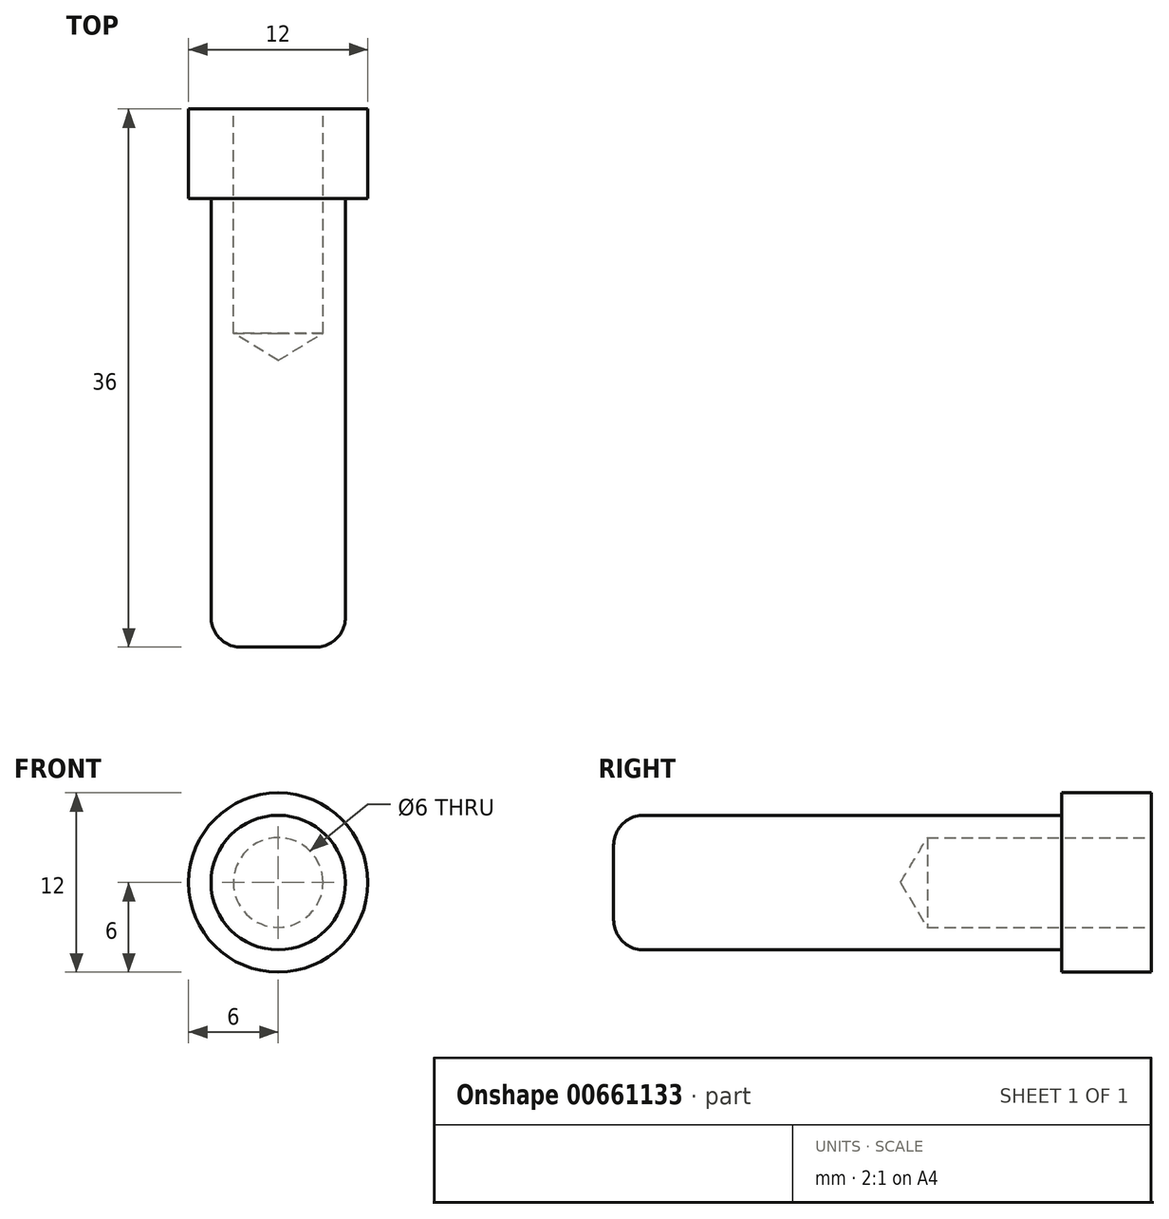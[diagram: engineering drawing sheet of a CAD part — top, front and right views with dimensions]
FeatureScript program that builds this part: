
annotation { "Feature Type Name" : "Feature", "Feature Type Description" : "" }
export const myFeature = defineFeature(function(context is Context, id is Id, definition is map)
    precondition{}
    {
        {
            var Q0;
            Q0=qCreatedBy(makeId("Front.planeOp"),FACE);
            var sketch = newSketch(context, id + "F0", { "sketchPlane" : qUnion([Q0])});
            skCircle(sketch, "E0", {"center": v(0, 0) * mm, "radius": 6 * mm});
            skSolve(sketch);
        }
        {
            var Q0;
            Q0 = qSketchRegion(id + "F0", true);
            extrude(context, id + "F1", {"entities" : qUnion([Q0]), "depth" : 6 * mm, "offsetDistance" : 25 * mm});
        }
        {
            var Q0;
            Q0=makeQuery(id+"F1.opExtrude","CAP_FACE",FACE,{"disambiguationData":[OSD([sQuery(id+"F0.wireOp",EDGE,"E0")])],"isStart":false});
            var sketch = newSketch(context, id + "F2", { "sketchPlane" : qUnion([Q0])});
            skCircle(sketch, "E1", {"center": v(0, 0) * mm, "radius": 4.5 * mm});
            skSolve(sketch);
        }
        {
            var Q0;
            Q0=makeQuery(id+"F2.imprint","IMPRINT",FACE,{"disambiguationData":[TD([[makeQuery(id+"F2.imprint","IMPRINT",EDGE,{"derivedFrom":sQuery(id+"F2.wireOp",EDGE,"E1")}),1.0]])]});
            extrude(context, id + "F3", {"entities" : qUnion([Q0]), "operationType" : NewBodyOperationType.ADD, "depth" : 30 * mm, "offsetDistance" : 25 * mm});
        }
        {
            var Q0;
            Q0=makeQuery(id+"F3.opExtrude","CAP_EDGE",EDGE,{"disambiguationData":[OSD([sQuery(id+"F2.wireOp",EDGE,"E1")])],"isStart":false});
            fillet(context, id + "F4", {"entities" : qUnion([Q0]), "radius" : 2 * mm, "tangentPropagation" : true, "allowEdgeOverflow" : false});
        }
        {
            var Q0;
            Q0=makeQuery(id+"F1.opExtrude","CAP_FACE",FACE,{"disambiguationData":[OSD([sQuery(id+"F0.wireOp",EDGE,"E0")])],"isStart":true});
            var sketch = newSketch(context, id + "F5", { "sketchPlane" : qUnion([Q0])});
            skPoint(sketch, "E2", {"position": v(0, 0) * mm});
            skSolve(sketch);
        }
        {
            var Q0;
            Q0=sQuery(id+"F5.wireOp",VERTEX,"E2");
            var Q1;
            Q1=makeQuery(id+"F1.opExtrude","SWEPT_BODY",BODY,{"disambiguationData":[OSD([sQuery(id+"F0.wireOp",EDGE,"E0")])]});
            hole(context, id + "F6", {"style" : HoleStyle.SIMPLE, "endStyle" : HoleEndStyle.BLIND, "holeDiameter" : 6 * mm, "majorDiameter" : 5 * mm, "holeDepth" : 15 * mm, "isTappedThrough" : true, "tappedDepth" : 19 * mm, "tapClearance" : 3, "startFromSketch" : true, "locations" : qUnion([Q0]), "scope" : qUnion([Q1])});
        }
    });
